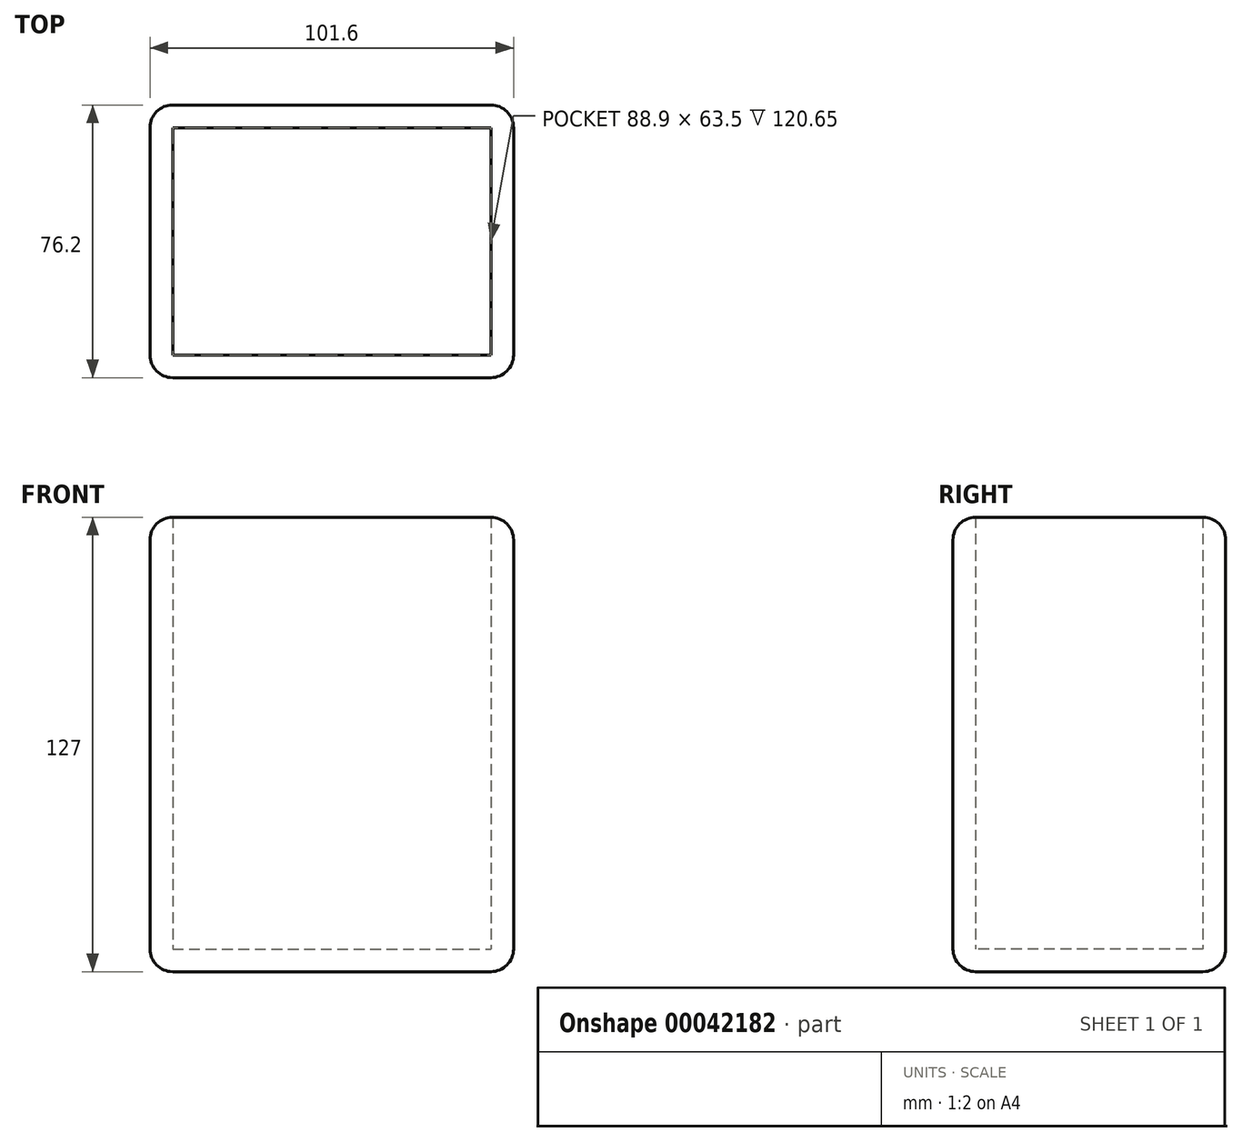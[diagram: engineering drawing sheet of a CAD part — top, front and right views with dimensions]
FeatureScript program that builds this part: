
annotation { "Feature Type Name" : "Feature", "Feature Type Description" : "" }
export const myFeature = defineFeature(function(context is Context, id is Id, definition is map)
    precondition{}
    {
        {
            var Q0;
            Q0=qCreatedBy(makeId("Top.planeOp"),FACE);
            var sketch = newSketch(context, id + "F0", { "sketchPlane" : qUnion([Q0])});
            skLineSegment(sketch, "E0.bottom", {"start": v(-57.5, 28.29) * mm, "end": v(44.1, 28.29) * mm});
            skLineSegment(sketch, "E0.top", {"start": v(-57.5, -47.91) * mm, "end": v(44.1, -47.91) * mm});
            skLineSegment(sketch, "E0.left", {"start": v(-57.5, 28.29) * mm, "end": v(-57.5, -47.91) * mm});
            skLineSegment(sketch, "E0.right", {"start": v(44.1, 28.29) * mm, "end": v(44.1, -47.91) * mm});
            skSolve(sketch);
        }
        {
            var Q0;
            Q0=makeQuery(id+"F0.imprint","IMPRINT",FACE,{"disambiguationData":[TD([[makeQuery(id+"F0.imprint","IMPRINT",EDGE,{"derivedFrom":sQuery(id+"F0.wireOp",EDGE,"E0.bottom")}),-1.0]])]});
            extrude(context, id + "F1", {"entities" : qUnion([Q0]), "depth" : 127 * mm});
        }
        {
            var Q0;
            Q0=makeQuery(id+"F1.opExtrude","CAP_FACE",FACE,{"disambiguationData":[OSD([sQuery(id+"F0.wireOp",EDGE,"E0.bottom"),sQuery(id+"F0.wireOp",EDGE,"E0.top"),sQuery(id+"F0.wireOp",EDGE,"E0.left"),sQuery(id+"F0.wireOp",EDGE,"E0.right")])],"isStart":false});
            shell(context, id + "F2", {"entities" : qUnion([Q0]), "thickness" : 6.35 * mm});
        }
        {
            var Q0;
            Q0=makeQuery(id+"F1.opExtrude","SWEPT_EDGE",EDGE,{"disambiguationData":[OSD([sQuery(id+"F0.wireOp",EDGE,"E0.top"),sQuery(id+"F0.wireOp",EDGE,"E0.left")])]});
            var Q1;
            Q1=makeQuery(id+"F1.opExtrude","SWEPT_FACE",FACE,{"disambiguationData":[OSD([sQuery(id+"F0.wireOp",EDGE,"E0.left")])]});
            var Q2;
            Q2=makeQuery(id+"F1.opExtrude","SWEPT_FACE",FACE,{"disambiguationData":[OSD([sQuery(id+"F0.wireOp",EDGE,"E0.bottom")])]});
            var Q3;
            Q3=makeQuery(id+"F1.opExtrude","SWEPT_FACE",FACE,{"disambiguationData":[OSD([sQuery(id+"F0.wireOp",EDGE,"E0.right")])]});
            var Q4;
            Q4=makeQuery(id+"F1.opExtrude","SWEPT_FACE",FACE,{"disambiguationData":[OSD([sQuery(id+"F0.wireOp",EDGE,"E0.top")])]});
            var Q5;
            Q5=makeQuery(id+"F1.opExtrude","CAP_EDGE",EDGE,{"disambiguationData":[OSD([sQuery(id+"F0.wireOp",EDGE,"E0.left")])],"isStart":true});
            fillet(context, id + "F3", {"entities" : qUnion([Q0, Q1, Q2, Q3, Q4, Q5]), "radius" : 6.35 * mm, "tangentPropagation" : true, "allowEdgeOverflow" : false});
        }
    });
